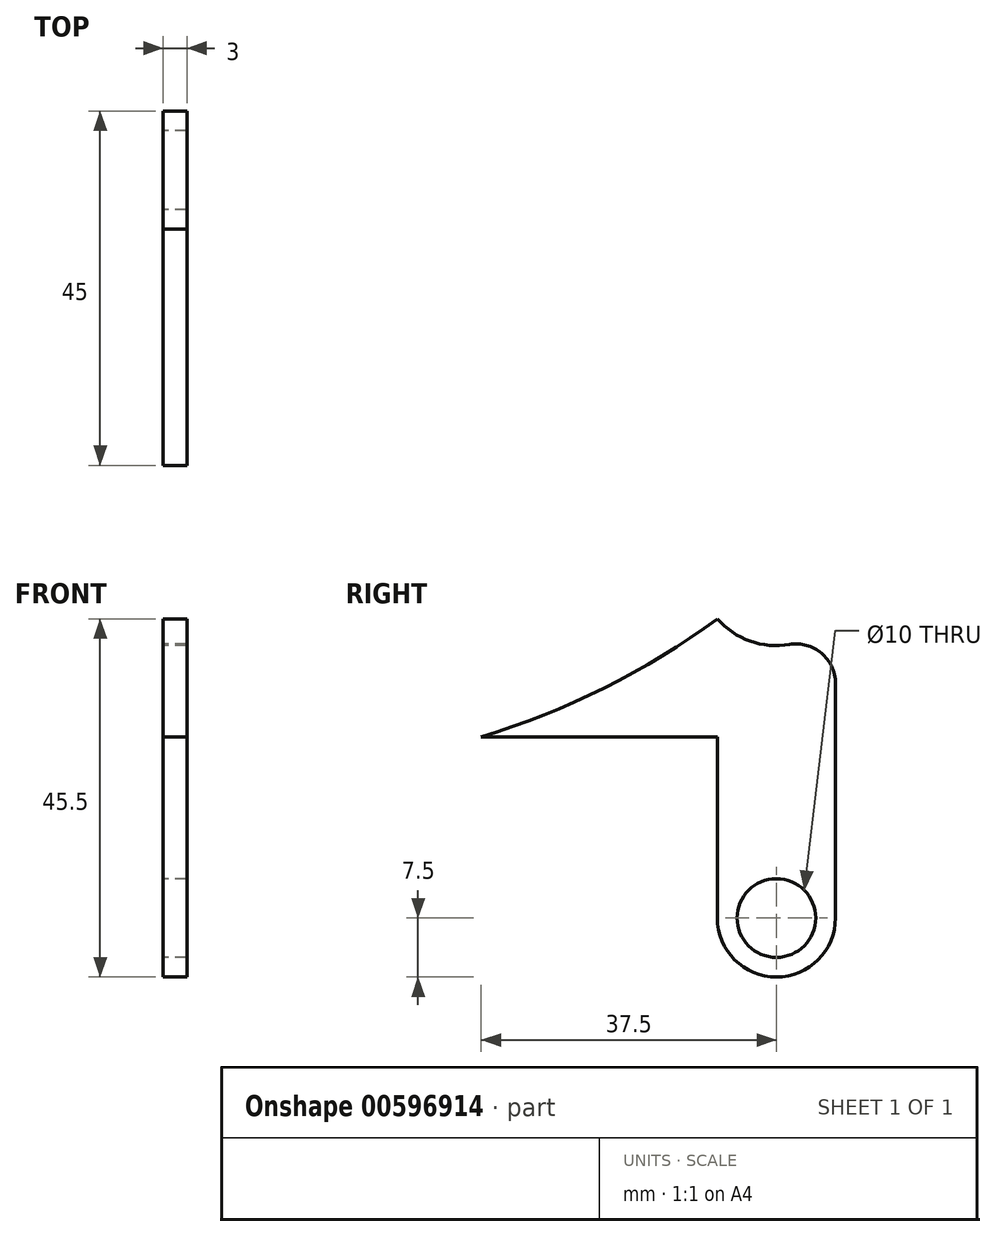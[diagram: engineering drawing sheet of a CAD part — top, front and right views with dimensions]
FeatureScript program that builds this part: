
annotation { "Feature Type Name" : "Feature", "Feature Type Description" : "" }
export const myFeature = defineFeature(function(context is Context, id is Id, definition is map)
    precondition{}
    {
        {
            var Q0;
            Q0=qCreatedBy(makeId("Right.planeOp"),FACE);
            var sketch = newSketch(context, id + "F0", { "sketchPlane" : qUnion([Q0])});
            skLineSegment(sketch, "E0", {"start": v(0, 0) * mm, "end": v(30, 0) * mm});
            skLineSegment(sketch, "E1", {"start": v(30, 0) * mm, "end": v(30, 15) * mm, "construction": true});
            skArc(sketch, "E2", {"start": v(0, 0) * mm, "mid": v(15.63, 6.23) * mm, "end": v(30, 15) * mm});
            skLineSegment(sketch, "E3", {"start": v(30, 0) * mm, "end": v(30, -23) * mm});
            skPoint(sketch, "E4.visualSharp", {"position": v(45, 15) * mm});
            skCircle(sketch, "E5", {"center": v(37.5, -23) * mm, "radius": 5 * mm});
            skArc(sketch, "E6.0", {"start": v(30, -23) * mm, "mid": v(37.5, -30.5) * mm, "end": v(45, -23) * mm});
            skLineSegment(sketch, "E7", {"start": v(45, -23) * mm, "end": v(45, 6.82) * mm});
            skArc(sketch, "E8", {"start": v(30, 15) * mm, "mid": v(34.16, 12.19) * mm, "end": v(39.17, 11.75) * mm});
            skArc(sketch, "E9.filletArc", {"start": v(45, 6.82) * mm, "mid": v(43.23, 10.64) * mm, "end": v(39.17, 11.75) * mm});
            skSolve(sketch);
        }
        {
            var Q0;
            Q0=makeQuery(id+"F0.imprint","IMPRINT",FACE,{"disambiguationData":[TD([[makeQuery(id+"F0.imprint","IMPRINT",EDGE,{"derivedFrom":sQuery(id+"F0.wireOp",EDGE,"E0")}),1.0]])]});
            extrude(context, id + "F1", {"entities" : qUnion([Q0]), "depth" : 3 * mm, "offsetDistance" : 25 * mm});
        }
    });
